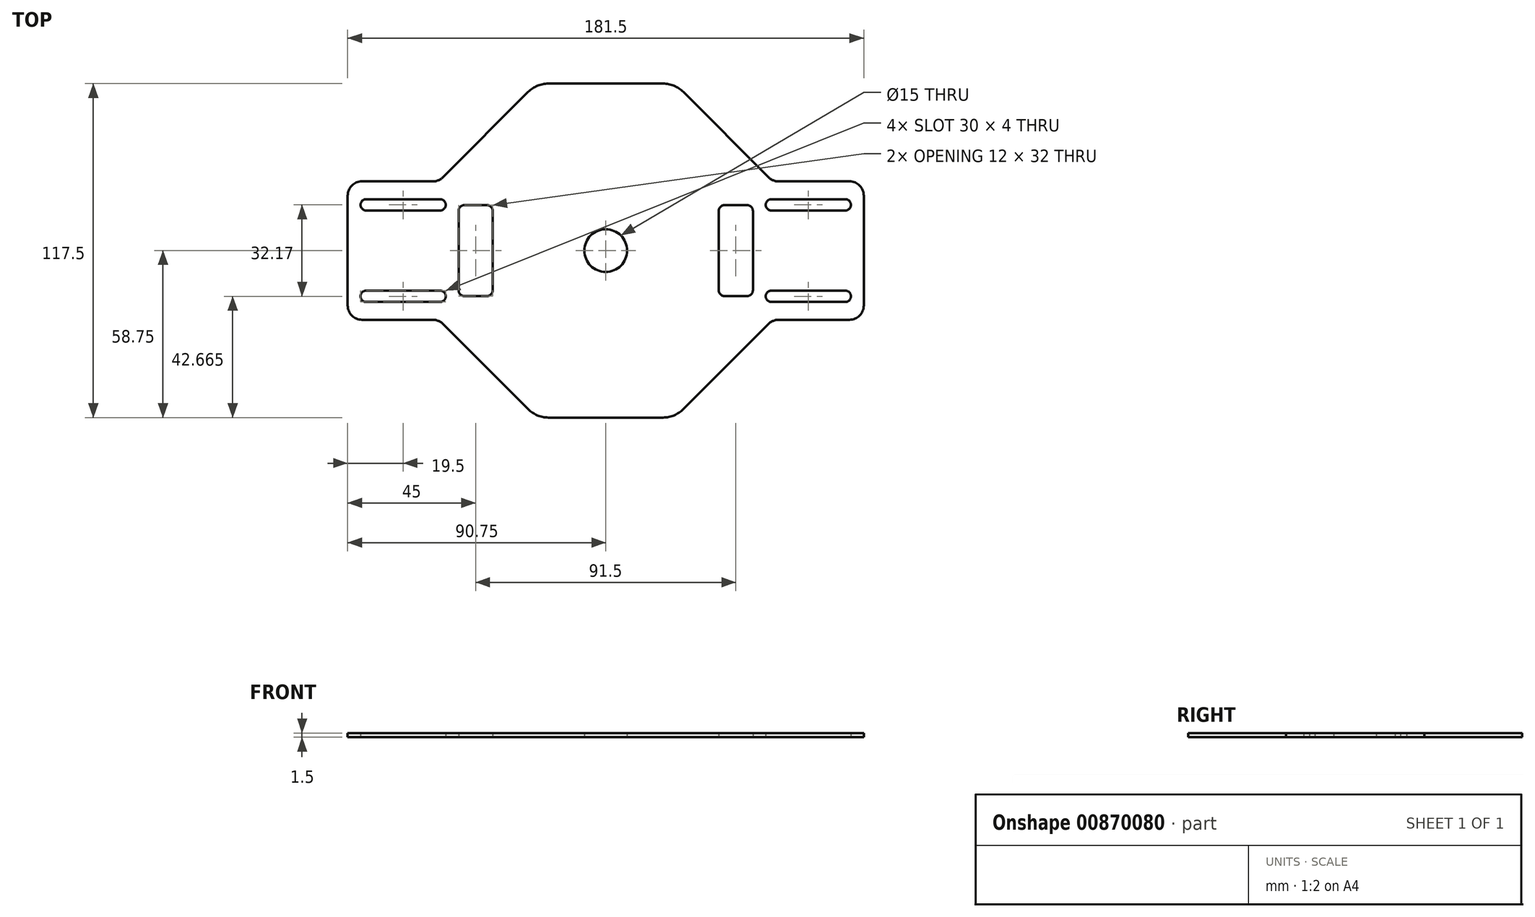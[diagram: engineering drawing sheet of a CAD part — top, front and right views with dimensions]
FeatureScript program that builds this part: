
annotation { "Feature Type Name" : "Feature", "Feature Type Description" : "" }
export const myFeature = defineFeature(function(context is Context, id is Id, definition is map)
    precondition{}
    {
        {
            var Q0;
            Q0=qCreatedBy(makeId("Top.planeOp"),FACE);
            var sketch = newSketch(context, id + "F0", { "sketchPlane" : qUnion([Q0])});
            skCircle(sketch, "E0.cCircle", {"center": v(0, 0) * mm, "radius": 58.75 * mm, "construction": true});
            skLineSegment(sketch, "E0.0", {"start": v(58.75, 24.34) * mm, "end": v(58.75, -24.34) * mm});
            skLineSegment(sketch, "E0.1", {"start": v(57.29, -25.8) * mm, "end": v(27.26, -55.82) * mm});
            skLineSegment(sketch, "E0.2", {"start": v(20.2, -58.75) * mm, "end": v(-20.2, -58.75) * mm});
            skLineSegment(sketch, "E0.3", {"start": v(-27.26, -55.82) * mm, "end": v(-57.29, -25.8) * mm});
            skLineSegment(sketch, "E0.4", {"start": v(-58.75, -24.34) * mm, "end": v(-58.75, 24.34) * mm});
            skLineSegment(sketch, "E0.5", {"start": v(-57.29, 25.8) * mm, "end": v(-27.26, 55.82) * mm});
            skLineSegment(sketch, "E0.6", {"start": v(-20.2, 58.75) * mm, "end": v(20.2, 58.75) * mm});
            skLineSegment(sketch, "E0.7", {"start": v(27.26, 55.82) * mm, "end": v(57.29, 25.8) * mm});
            skPoint(sketch, "E0.0.midPoint", {"position": v(58.75, 0) * mm});
            skLineSegment(sketch, "E1.bottom", {"start": v(60.82, 24.34) * mm, "end": v(85.75, 24.34) * mm});
            skLineSegment(sketch, "E1.top", {"start": v(60.82, -24.34) * mm, "end": v(85.75, -24.34) * mm});
            skLineSegment(sketch, "E1.right", {"start": v(90.75, 19.34) * mm, "end": v(90.75, -19.34) * mm});
            skLineSegment(sketch, "E2.bottom", {"start": v(-60.82, 24.34) * mm, "end": v(-85.75, 24.34) * mm});
            skLineSegment(sketch, "E2.top", {"start": v(-60.82, -24.34) * mm, "end": v(-85.75, -24.34) * mm});
            skLineSegment(sketch, "E2.left", {"start": v(-58.75, 24.34) * mm, "end": v(-58.75, -24.34) * mm});
            skLineSegment(sketch, "E2.right", {"start": v(-90.75, 19.34) * mm, "end": v(-90.75, -19.34) * mm});
            skPoint(sketch, "E3.visualSharp", {"position": v(-58.75, 24.34) * mm});
            skArc(sketch, "E3.filletArc", {"start": v(-60.82, 24.34) * mm, "mid": v(-58.9, 24.72) * mm, "end": v(-57.29, 25.8) * mm});
            skPoint(sketch, "E4.visualSharp", {"position": v(58.75, 24.34) * mm});
            skArc(sketch, "E4.filletArc", {"start": v(57.29, 25.8) * mm, "mid": v(58.9, 24.72) * mm, "end": v(60.82, 24.34) * mm});
            skPoint(sketch, "E5.visualSharp", {"position": v(24.34, 58.75) * mm});
            skArc(sketch, "E5.filletArc", {"start": v(27.26, 55.82) * mm, "mid": v(24.02, 57.99) * mm, "end": v(20.2, 58.75) * mm});
            skPoint(sketch, "E6.visualSharp", {"position": v(-24.34, 58.75) * mm});
            skArc(sketch, "E6.filletArc", {"start": v(-20.2, 58.75) * mm, "mid": v(-24.02, 57.99) * mm, "end": v(-27.26, 55.82) * mm});
            skPoint(sketch, "E7.visualSharp", {"position": v(24.34, -58.75) * mm});
            skArc(sketch, "E7.filletArc", {"start": v(20.2, -58.75) * mm, "mid": v(24.02, -57.99) * mm, "end": v(27.26, -55.82) * mm});
            skPoint(sketch, "E8.visualSharp", {"position": v(-24.34, -58.75) * mm});
            skArc(sketch, "E8.filletArc", {"start": v(-27.26, -55.82) * mm, "mid": v(-24.02, -57.99) * mm, "end": v(-20.2, -58.75) * mm});
            skPoint(sketch, "E9.visualSharp", {"position": v(-58.75, -24.34) * mm});
            skArc(sketch, "E9.filletArc", {"start": v(-57.29, -25.8) * mm, "mid": v(-58.9, -24.72) * mm, "end": v(-60.82, -24.34) * mm});
            skPoint(sketch, "E10.visualSharp", {"position": v(58.75, -24.34) * mm});
            skArc(sketch, "E10.filletArc", {"start": v(60.82, -24.34) * mm, "mid": v(58.9, -24.72) * mm, "end": v(57.29, -25.8) * mm});
            skPoint(sketch, "E11.visualSharp", {"position": v(90.75, -24.34) * mm});
            skArc(sketch, "E11.filletArc", {"start": v(85.75, -24.34) * mm, "mid": v(89.29, -22.87) * mm, "end": v(90.75, -19.34) * mm});
            skPoint(sketch, "E12.visualSharp", {"position": v(90.75, 24.34) * mm});
            skArc(sketch, "E12.filletArc", {"start": v(90.75, 19.34) * mm, "mid": v(89.29, 22.87) * mm, "end": v(85.75, 24.34) * mm});
            skPoint(sketch, "E13.visualSharp", {"position": v(-90.75, 24.34) * mm});
            skArc(sketch, "E13.filletArc", {"start": v(-85.75, 24.34) * mm, "mid": v(-89.29, 22.87) * mm, "end": v(-90.75, 19.34) * mm});
            skPoint(sketch, "E14.visualSharp", {"position": v(-90.75, -24.34) * mm});
            skArc(sketch, "E14.filletArc", {"start": v(-90.75, -19.34) * mm, "mid": v(-89.29, -22.87) * mm, "end": v(-85.75, -24.34) * mm});
            skLineSegment(sketch, "E15", {"start": v(-80.5, -24.34) * mm, "end": v(-80.5, -18.09) * mm});
            skLineSegment(sketch, "E16", {"start": v(-58.25, -18.09) * mm, "end": v(-84.25, -18.09) * mm});
            skLineSegment(sketch, "E17", {"start": v(-56.25, -16.09) * mm, "end": v(-56.25, -16.09) * mm});
            skLineSegment(sketch, "E18", {"start": v(-58.25, -14.09) * mm, "end": v(-84.25, -14.09) * mm});
            skLineSegment(sketch, "E19", {"start": v(-86.25, -16.09) * mm, "end": v(-86.25, -16.09) * mm});
            skLineSegment(sketch, "E20", {"start": v(-86.25, -14.09) * mm, "end": v(-90.75, -14.09) * mm});
            skLineSegment(sketch, "E21", {"start": v(-90.75, 0) * mm, "end": v(90.75, 0) * mm});
            skLineSegment(sketch, "E22", {"start": v(0, 58.75) * mm, "end": v(0, -58.75) * mm});
            skPoint(sketch, "E23.visualSharp", {"position": v(-86.25, -14.09) * mm});
            skArc(sketch, "E23.filletArc", {"start": v(-85.7, -14.09) * mm, "mid": v(-86.09, -14.25) * mm, "end": v(-86.25, -14.63) * mm});
            skArc(sketch, "E24.filletArc", {"start": v(-84.25, -14.09) * mm, "mid": v(-85.66, -14.67) * mm, "end": v(-86.25, -16.09) * mm});
            skPoint(sketch, "E25.visualSharp", {"position": v(-86.25, -18.09) * mm});
            skArc(sketch, "E25.filletArc", {"start": v(-86.25, -16.09) * mm, "mid": v(-85.66, -17.5) * mm, "end": v(-84.25, -18.09) * mm});
            skPoint(sketch, "E26.visualSharp", {"position": v(-56.25, -18.09) * mm});
            skArc(sketch, "E26.filletArc", {"start": v(-58.25, -18.09) * mm, "mid": v(-56.84, -17.5) * mm, "end": v(-56.25, -16.09) * mm});
            skPoint(sketch, "E27.visualSharp", {"position": v(-56.25, -14.09) * mm});
            skArc(sketch, "E27.filletArc", {"start": v(-56.25, -16.09) * mm, "mid": v(-56.84, -14.67) * mm, "end": v(-58.25, -14.09) * mm});
            skLineSegment(sketch, "E28.MirrorCS", {"start": v(-58.25, 14.09) * mm, "end": v(-84.25, 14.09) * mm});
            skArc(sketch, "E29.MirrorCS", {"start": v(-56.25, 16.09) * mm, "mid": v(-56.84, 14.67) * mm, "end": v(-58.25, 14.09) * mm});
            skArc(sketch, "E30.MirrorCS", {"start": v(-58.25, 18.09) * mm, "mid": v(-56.84, 17.5) * mm, "end": v(-56.25, 16.09) * mm});
            skLineSegment(sketch, "E31.MirrorCS", {"start": v(-58.25, 18.09) * mm, "end": v(-84.25, 18.09) * mm});
            skArc(sketch, "E32.MirrorCS", {"start": v(-86.25, 16.09) * mm, "mid": v(-85.66, 17.5) * mm, "end": v(-84.25, 18.09) * mm});
            skArc(sketch, "E33.MirrorCS", {"start": v(-84.25, 14.09) * mm, "mid": v(-85.66, 14.67) * mm, "end": v(-86.25, 16.09) * mm});
            skArc(sketch, "E34.MirrorCS", {"start": v(58.25, -18.09) * mm, "mid": v(56.84, -17.5) * mm, "end": v(56.25, -16.09) * mm});
            skArc(sketch, "E35.MirrorCS", {"start": v(56.25, -16.09) * mm, "mid": v(56.84, -14.67) * mm, "end": v(58.25, -14.09) * mm});
            skLineSegment(sketch, "E36.MirrorCS", {"start": v(58.25, -14.09) * mm, "end": v(84.25, -14.09) * mm});
            skArc(sketch, "E37.MirrorCS", {"start": v(84.25, -14.09) * mm, "mid": v(85.66, -14.67) * mm, "end": v(86.25, -16.09) * mm});
            skArc(sketch, "E38.MirrorCS", {"start": v(86.25, -16.09) * mm, "mid": v(85.66, -17.5) * mm, "end": v(84.25, -18.09) * mm});
            skLineSegment(sketch, "E39.MirrorCS", {"start": v(58.25, -18.09) * mm, "end": v(84.25, -18.09) * mm});
            skArc(sketch, "E40.MirrorCS", {"start": v(56.25, 16.09) * mm, "mid": v(56.84, 14.67) * mm, "end": v(58.25, 14.09) * mm});
            skArc(sketch, "E41.MirrorCS", {"start": v(58.25, 18.09) * mm, "mid": v(56.84, 17.5) * mm, "end": v(56.25, 16.09) * mm});
            skLineSegment(sketch, "E42.MirrorCS", {"start": v(58.25, 18.09) * mm, "end": v(84.25, 18.09) * mm});
            skArc(sketch, "E43.MirrorCS", {"start": v(86.25, 16.09) * mm, "mid": v(85.66, 17.5) * mm, "end": v(84.25, 18.09) * mm});
            skArc(sketch, "E44.MirrorCS", {"start": v(84.25, 14.09) * mm, "mid": v(85.66, 14.67) * mm, "end": v(86.25, 16.09) * mm});
            skLineSegment(sketch, "E45.MirrorCS", {"start": v(58.25, 14.09) * mm, "end": v(84.25, 14.09) * mm});
            skLineSegment(sketch, "E46.bottom", {"start": v(-41.75, -16) * mm, "end": v(-49.75, -16) * mm});
            skLineSegment(sketch, "E46.top", {"start": v(-41.75, 16) * mm, "end": v(-49.75, 16) * mm});
            skLineSegment(sketch, "E46.left", {"start": v(-39.75, -14) * mm, "end": v(-39.75, 14) * mm});
            skLineSegment(sketch, "E46.right", {"start": v(-51.75, -14) * mm, "end": v(-51.75, 14) * mm});
            skPoint(sketch, "E46.middle", {"position": v(-45.75, 0) * mm});
            skLineSegment(sketch, "E47", {"start": v(-51.75, 0) * mm, "end": v(-90.75, 0) * mm});
            skPoint(sketch, "E48.visualSharp", {"position": v(-51.75, 16) * mm});
            skArc(sketch, "E48.filletArc", {"start": v(-49.75, 16) * mm, "mid": v(-51.16, 15.41) * mm, "end": v(-51.75, 14) * mm});
            skPoint(sketch, "E49.visualSharp", {"position": v(-39.75, 16) * mm});
            skArc(sketch, "E49.filletArc", {"start": v(-39.75, 14) * mm, "mid": v(-40.34, 15.41) * mm, "end": v(-41.75, 16) * mm});
            skPoint(sketch, "E50.visualSharp", {"position": v(-39.75, -16) * mm});
            skArc(sketch, "E50.filletArc", {"start": v(-41.75, -16) * mm, "mid": v(-40.34, -15.41) * mm, "end": v(-39.75, -14) * mm});
            skPoint(sketch, "E51.visualSharp", {"position": v(-51.75, -16) * mm});
            skArc(sketch, "E51.filletArc", {"start": v(-51.75, -14) * mm, "mid": v(-51.16, -15.41) * mm, "end": v(-49.75, -16) * mm});
            skLineSegment(sketch, "E52.MirrorCS", {"start": v(39.75, -14) * mm, "end": v(39.75, 14) * mm});
            skArc(sketch, "E53.MirrorCS", {"start": v(39.75, 14) * mm, "mid": v(40.34, 15.41) * mm, "end": v(41.75, 16) * mm});
            skLineSegment(sketch, "E54.MirrorCS", {"start": v(41.75, 16) * mm, "end": v(49.75, 16) * mm});
            skArc(sketch, "E55.MirrorCS", {"start": v(49.75, 16) * mm, "mid": v(51.16, 15.41) * mm, "end": v(51.75, 14) * mm});
            skLineSegment(sketch, "E56.MirrorCS", {"start": v(51.75, -14) * mm, "end": v(51.75, 14) * mm});
            skArc(sketch, "E57.MirrorCS", {"start": v(51.75, -14) * mm, "mid": v(51.16, -15.41) * mm, "end": v(49.75, -16) * mm});
            skLineSegment(sketch, "E58.MirrorCS", {"start": v(41.75, -16) * mm, "end": v(49.75, -16) * mm});
            skArc(sketch, "E59.MirrorCS", {"start": v(41.75, -16) * mm, "mid": v(40.34, -15.41) * mm, "end": v(39.75, -14) * mm});
            skCircle(sketch, "E60", {"center": v(0, 0) * mm, "radius": 7.5 * mm});
            skSolve(sketch);
        }
        {
            var Q0;
            {var subQ88=sQuery(id+"F0.wireOp",EDGE,"E14.filletArc");Q0=qUnion([makeQuery(id+"F0.imprint","IMPRINT",FACE,{"disambiguationData":[TD([[makeQuery(id+"F0.imprint","IMPRINT",EDGE,{"derivedFrom":subQ88}),1.0]])]}),makeQuery(id+"F0.imprint","IMPRINT",FACE,{"disambiguationData":[TD([[makeQuery(id+"F0.imprint","IMPRINT",EDGE,{"derivedFrom":sQuery(id+"F0.wireOp",EDGE,"E0.1")}),-1.0]])]}),makeQuery(id+"F0.imprint","IMPRINT",FACE,{"disambiguationData":[TD([[makeQuery(id+"F0.imprint","IMPRINT",EDGE,{"derivedFrom":sQuery(id+"F0.wireOp",EDGE,"E0.7")}),-1.0]])]}),makeQuery(id+"F0.imprint","IMPRINT",FACE,{"disambiguationData":[TD([[makeQuery(id+"F0.imprint","IMPRINT",EDGE,{"derivedFrom":sQuery(id+"F0.wireOp",EDGE,"E0.3")}),-1.0]])]}),makeQuery(id+"F0.imprint","IMPRINT",FACE,{"disambiguationData":[TD([[makeQuery(id+"F0.imprint","IMPRINT",EDGE,{"derivedFrom":sQuery(id+"F0.wireOp",EDGE,"E0.5")}),-1.0]])]})]);}
            extrude(context, id + "F1", {"entities" : qUnion([Q0]), "depth" : 1.5 * mm, "offsetDistance" : 25 * mm});
        }
    });
